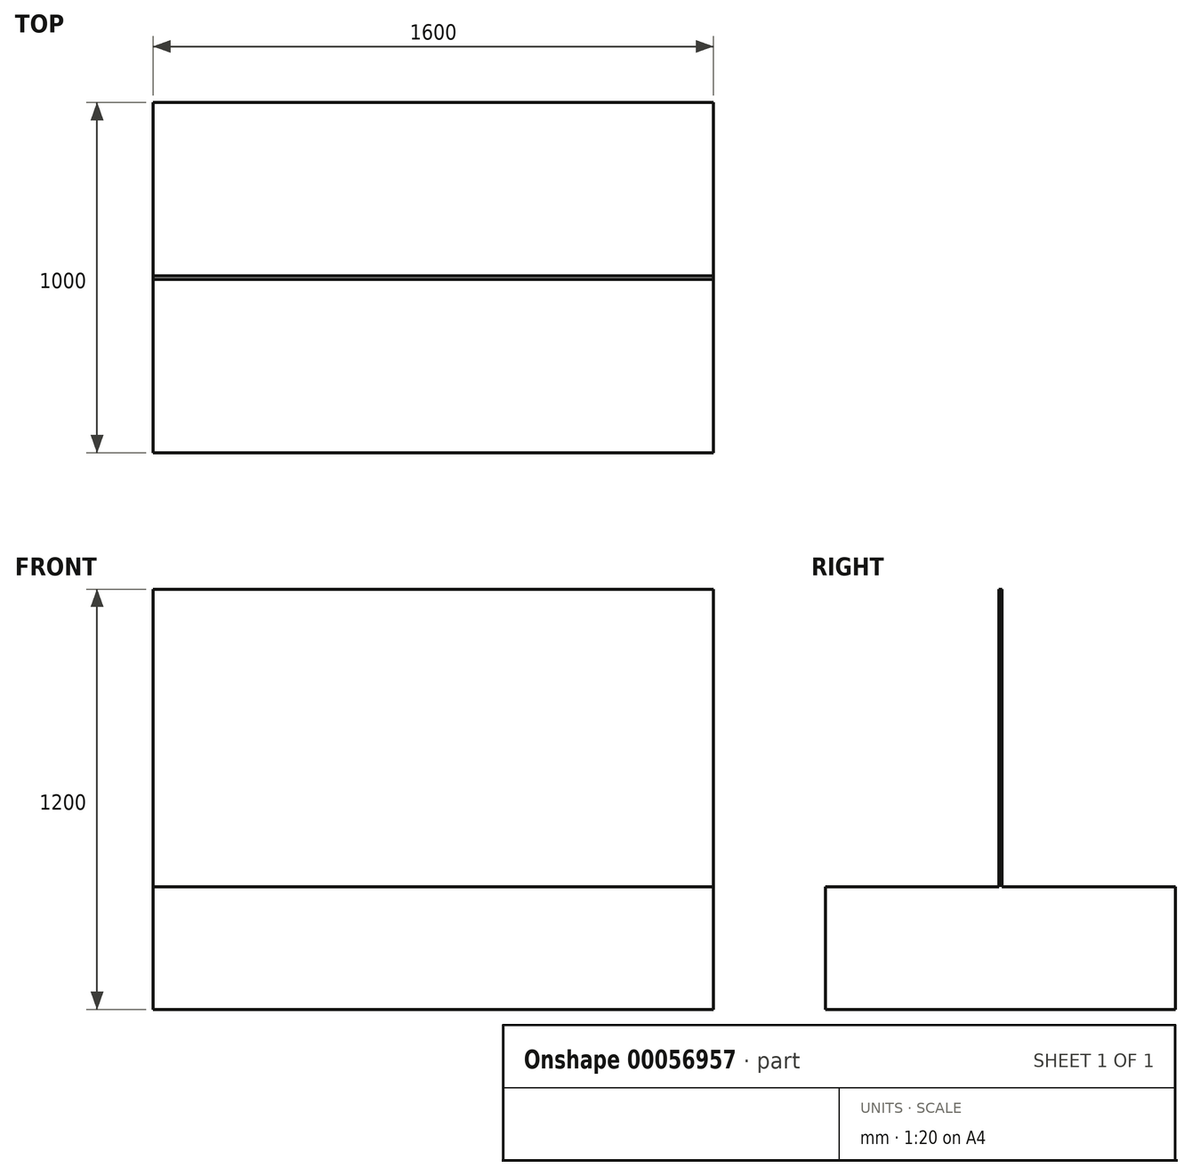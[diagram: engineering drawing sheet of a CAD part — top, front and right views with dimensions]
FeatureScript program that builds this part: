
annotation { "Feature Type Name" : "Feature", "Feature Type Description" : "" }
export const myFeature = defineFeature(function(context is Context, id is Id, definition is map)
    precondition{}
    {
        {
            var Q0;
            Q0=qCreatedBy(makeId("Top.planeOp"),FACE);
            var sketch = newSketch(context, id + "F0", { "sketchPlane" : qUnion([Q0])});
            skLineSegment(sketch, "E0.bottom", {"start": v(0, 0) * mm, "end": v(-1600, 0) * mm});
            skLineSegment(sketch, "E0.top", {"start": v(0, -1000) * mm, "end": v(-1600, -1000) * mm});
            skLineSegment(sketch, "E0.left", {"start": v(0, 0) * mm, "end": v(0, -1000) * mm});
            skLineSegment(sketch, "E0.right", {"start": v(-1600, 0) * mm, "end": v(-1600, -1000) * mm});
            skLineSegment(sketch, "E1", {"start": v(0, -500) * mm, "end": v(-1600, -500) * mm});
            skLineSegment(sketch, "E2", {"start": v(-1600, -495) * mm, "end": v(0, -495) * mm});
            skLineSegment(sketch, "E3", {"start": v(-1600, -505) * mm, "end": v(0, -505) * mm});
            skSolve(sketch);
        }
        {
            var Q0;
            {var subQ0=sQuery(id+"F0.wireOp",EDGE,"E1");Q0=makeQuery(id+"F0.imprint","IMPRINT",FACE,{"disambiguationData":[TD([[makeQuery(id+"F0.imprint","IMPRINT",EDGE,{"derivedFrom":subQ0}),-1.0]])]});}
            var Q1;
            {var subQ0=sQuery(id+"F0.wireOp",EDGE,"E1");Q1=makeQuery(id+"F0.imprint","IMPRINT",FACE,{"disambiguationData":[TD([[makeQuery(id+"F0.imprint","IMPRINT",EDGE,{"derivedFrom":subQ0}),1.0]])]});}
            extrude(context, id + "F1", {"entities" : qUnion([Q0, Q1]), "depth" : 1200 * mm});
        }
        {
            var Q0;
            Q0 = qSketchRegion(id + "F0", true);
            extrude(context, id + "F2", {"entities" : qUnion([Q0]), "operationType" : NewBodyOperationType.ADD, "depth" : 350 * mm});
        }
    });
